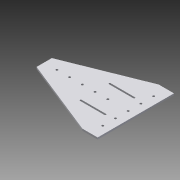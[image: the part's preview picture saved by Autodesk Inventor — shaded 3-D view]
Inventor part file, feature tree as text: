
AUTODESK INVENTOR PART (.ipt)
format: ipt  version: 2015 (Build 190159000, 159)  size: 165,888 bytes
history: native  units: in
note: dims shown in document units (in); Inventor stores cm internally (conversion verified against a paired STEP export)
features: other x5, hole x1, projected_geometry x1
ambient origin geometry x8: Origin, YZ Plane, XZ Plane, XY Plane, X Axis, Y Axis, Z Axis, Center Point
bodies: Solid1 (feature_tree)
feature tree (7):
  hole  "rivet_holes"  [1 undecoded]
  other  "face_sketch"
  other  "Plate1"
  other  "rivet_holes_sketch"
  projected_geometry  "Projected Loop1"
  other  "hm_mounting_slot_sketch"
  other  "Cut1"
note: 1 required parameter value undecoded (feature->parameter linkage not recoverable at this tier; creation-order binding heuristic only, values carry confidence <= 0.55)
